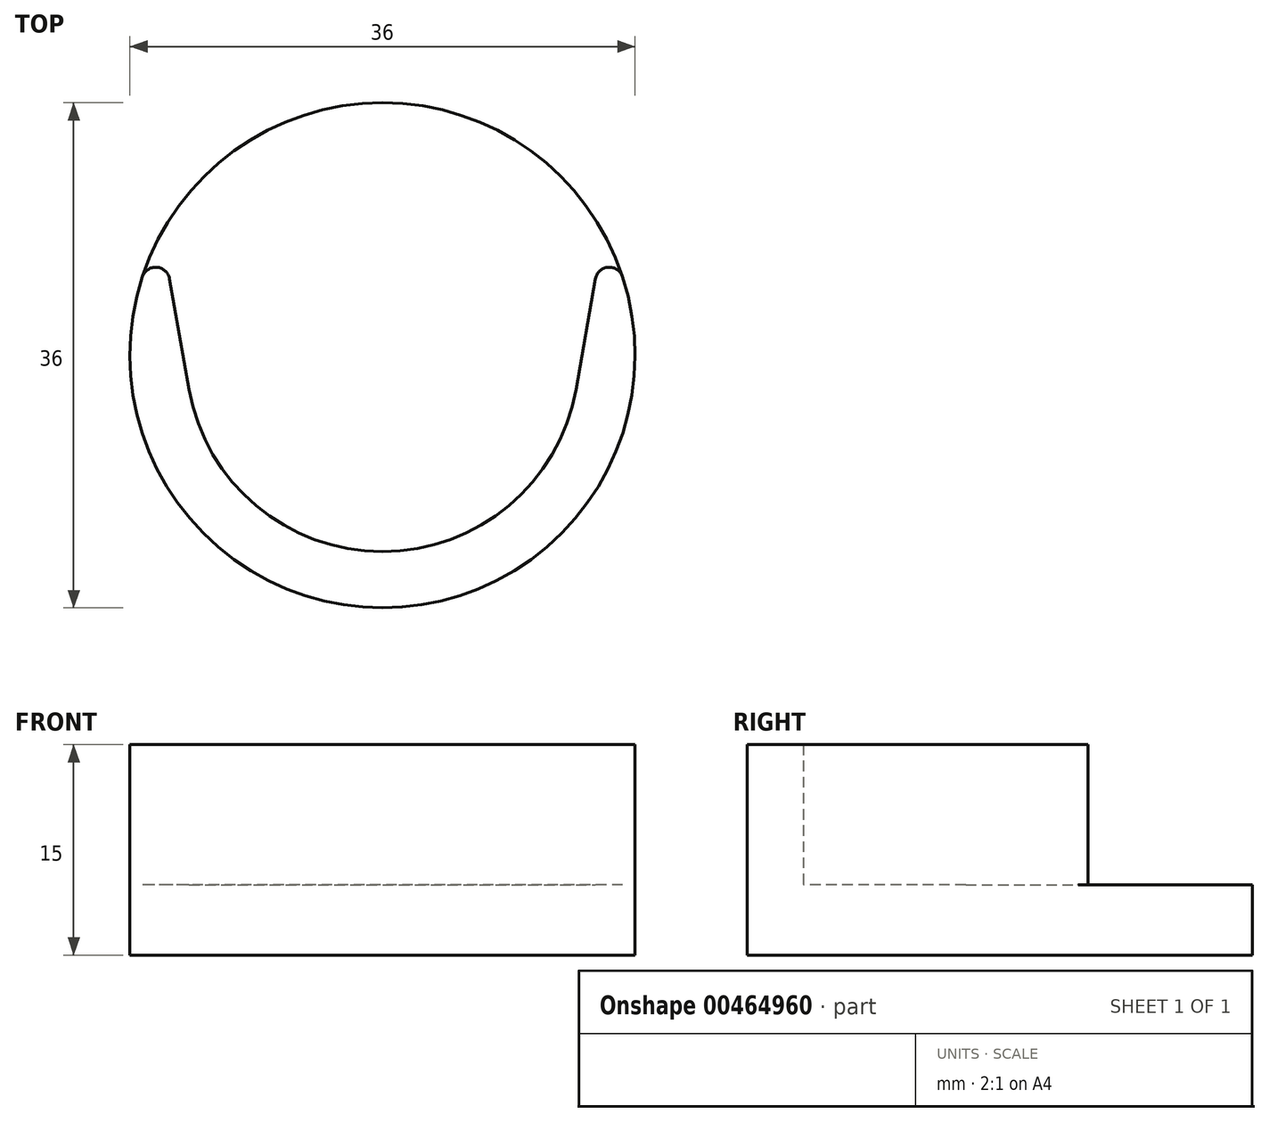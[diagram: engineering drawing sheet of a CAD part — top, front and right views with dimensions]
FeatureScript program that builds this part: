
annotation { "Feature Type Name" : "Feature", "Feature Type Description" : "" }
export const myFeature = defineFeature(function(context is Context, id is Id, definition is map)
    precondition{}
    {
        {
            var Q0;
            Q0=qCreatedBy(makeId("Top.planeOp"),FACE);
            var sketch = newSketch(context, id + "F0", { "sketchPlane" : qUnion([Q0])});
            skCircle(sketch, "E0", {"center": v(0, 0) * mm, "radius": 18 * mm});
            skCircle(sketch, "E1", {"center": v(0, 0) * mm, "radius": 14 * mm});
            skLineSegment(sketch, "E2", {"start": v(-10.72, -19.8) * mm, "end": v(-17.4, 18.03) * mm, "construction": true});
            skLineSegment(sketch, "E3.MirrorCS", {"start": v(10.72, -19.8) * mm, "end": v(17.4, 18.03) * mm, "construction": true});
            skLineSegment(sketch, "E4", {"start": v(-13.79, -2.43) * mm, "end": v(-15.75, 8.71) * mm});
            skLineSegment(sketch, "E5", {"start": v(13.79, -2.43) * mm, "end": v(15.75, 8.71) * mm});
            skSolve(sketch);
        }
        {
            var Q0;
            {var subQ0=sQuery(id+"F0.wireOp",EDGE,"E1");var subQ1=makeQuery(id+"F0.imprint","INTERSECT",VERTEX,{"derivedFrom":[subQ0,sQuery(id+"F0.wireOp",EDGE,"E4")]});Q0=makeQuery(id+"F0.imprint","IMPRINT",FACE,{"disambiguationData":[TD([[makeQuery(id+"F0.imprint","IMPRINT",EDGE,{"disambiguationData":[TD([[subQ1,-1.0]])],"derivedFrom":subQ0}),1.0]])]});}
            var Q1;
            {var subQ0=sQuery(id+"F0.wireOp",EDGE,"E4");Q1=makeQuery(id+"F0.imprint","IMPRINT",FACE,{"disambiguationData":[TD([[makeQuery(id+"F0.imprint","IMPRINT",EDGE,{"derivedFrom":subQ0}),-1.0]])]});}
            extrude(context, id + "F1", {"entities" : qUnion([Q0, Q1]), "depth" : 5 * mm});
        }
        {
            var Q0;
            {var subQ0=sQuery(id+"F0.wireOp",EDGE,"E4");Q0=makeQuery(id+"F0.imprint","IMPRINT",FACE,{"disambiguationData":[TD([[makeQuery(id+"F0.imprint","IMPRINT",EDGE,{"derivedFrom":subQ0}),1.0]])]});}
            extrude(context, id + "F2", {"entities" : qUnion([Q0]), "operationType" : NewBodyOperationType.ADD, "depth" : 15 * mm});
        }
        {
            var Q0;
            Q0=makeQuery(id+"F2.opExtrude","SWEPT_EDGE",EDGE,{"disambiguationData":[OSD([sQuery(id+"F0.wireOp",EDGE,"E0"),sQuery(id+"F0.wireOp",EDGE,"E4")])]});
            var Q1;
            Q1=makeQuery(id+"F2.opExtrude","SWEPT_EDGE",EDGE,{"disambiguationData":[OSD([sQuery(id+"F0.wireOp",EDGE,"E0"),sQuery(id+"F0.wireOp",EDGE,"E5")])]});
            fillet(context, id + "F3", {"entities" : qUnion([Q0, Q1]), "radius" : 1 * mm, "tangentPropagation" : true, "allowEdgeOverflow" : false});
        }
    });
